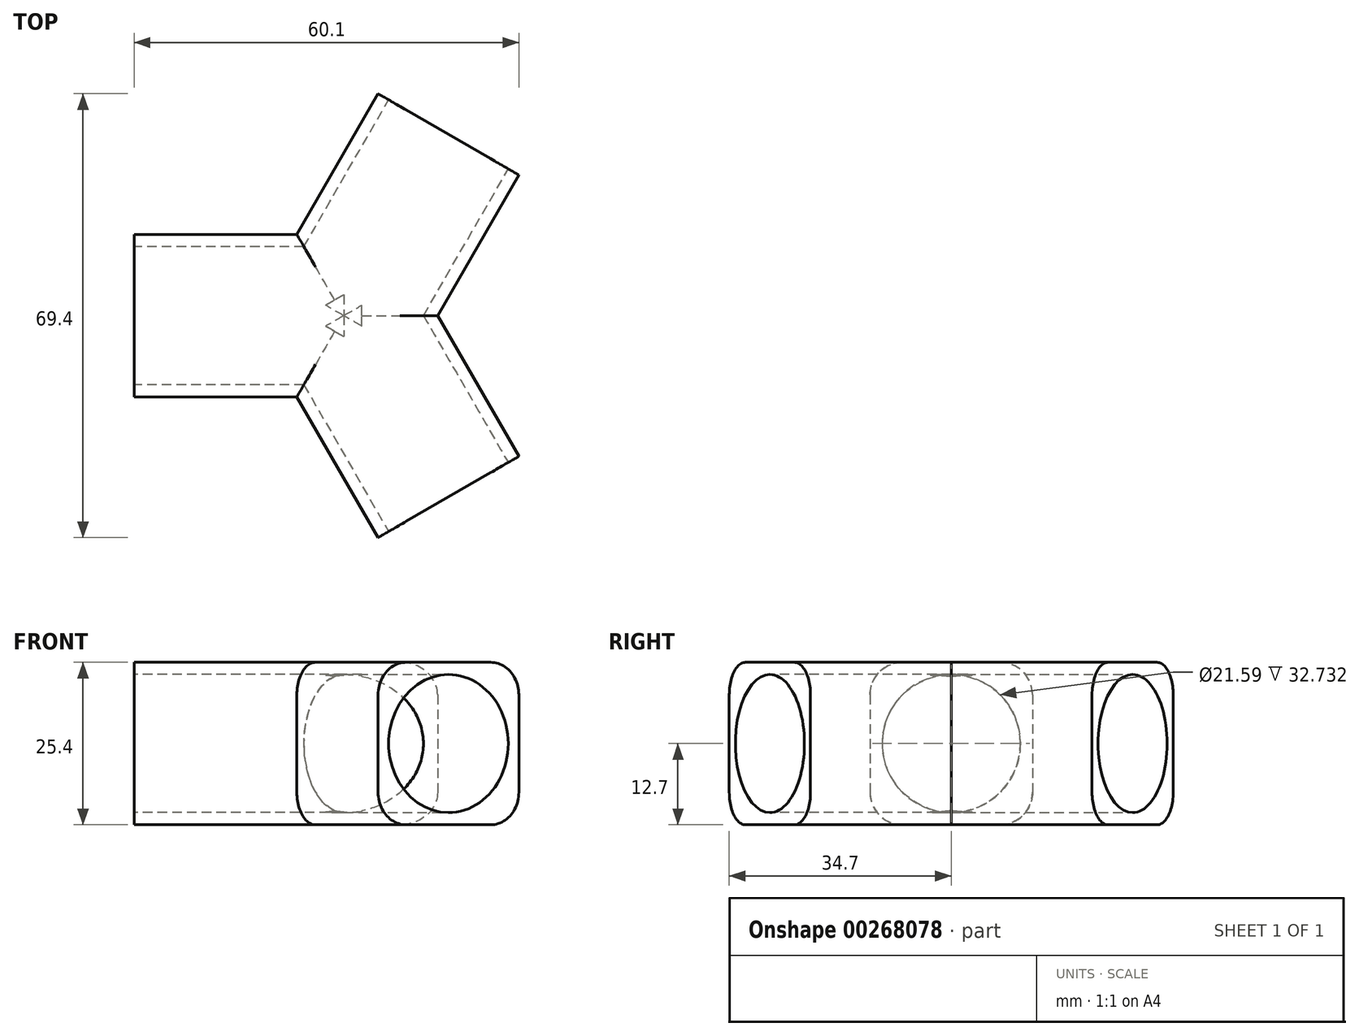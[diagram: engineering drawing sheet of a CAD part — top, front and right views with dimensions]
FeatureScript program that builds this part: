
annotation { "Feature Type Name" : "Feature", "Feature Type Description" : "" }
export const myFeature = defineFeature(function(context is Context, id is Id, definition is map)
    precondition{}
    {
        {
            var Q0;
            Q0=qCreatedBy(makeId("Top.planeOp"),FACE);
            var sketch = newSketch(context, id + "F0", { "sketchPlane" : qUnion([Q0])});
            skLineSegment(sketch, "E0.bottom", {"start": v(-5.96, 34.7) * mm, "end": v(16.04, 22) * mm});
            skLineSegment(sketch, "E0.top", {"start": v(-18.66, 12.7) * mm, "end": v(3.34, 0) * mm, "construction": true});
            skLineSegment(sketch, "E0.left", {"start": v(-5.96, 34.7) * mm, "end": v(-18.66, 12.7) * mm});
            skLineSegment(sketch, "E0.right", {"start": v(16.04, 22) * mm, "end": v(3.34, 0) * mm});
            skLineSegment(sketch, "E1.bottom", {"start": v(-44.06, 12.7) * mm, "end": v(-18.66, 12.7) * mm});
            skLineSegment(sketch, "E1.top", {"start": v(-44.06, -12.7) * mm, "end": v(-18.66, -12.7) * mm});
            skLineSegment(sketch, "E1.left", {"start": v(-44.06, 12.7) * mm, "end": v(-44.06, -12.7) * mm});
            skLineSegment(sketch, "E1.right", {"start": v(-18.66, 12.7) * mm, "end": v(-18.66, -12.7) * mm, "construction": true});
            skLineSegment(sketch, "E2.left", {"start": v(-18.66, -12.7) * mm, "end": v(3.34, 0) * mm, "construction": true});
            skLineSegment(sketch, "E3", {"start": v(-18.66, -12.7) * mm, "end": v(-5.96, -34.7) * mm});
            skLineSegment(sketch, "E4", {"start": v(-5.96, -34.7) * mm, "end": v(16.04, -22) * mm});
            skLineSegment(sketch, "E5", {"start": v(16.04, -22) * mm, "end": v(3.34, 0) * mm});
            skSolve(sketch);
        }
        {
            var Q0;
            Q0=makeQuery(id+"F0.imprint","IMPRINT",FACE,{"disambiguationData":[TD([[makeQuery(id+"F0.imprint","IMPRINT",EDGE,{"derivedFrom":sQuery(id+"F0.wireOp",EDGE,"E0.bottom")}),-1.0]])]});
            extrude(context, id + "F1", {"entities" : qUnion([Q0]), "depth" : 25.4 * mm});
        }
        {
            var Q0;
            Q0=makeQuery(id+"F1.opExtrude","SWEPT_FACE",FACE,{"disambiguationData":[OSD([sQuery(id+"F0.wireOp",EDGE,"E4")])]});
            var sketch = newSketch(context, id + "F2", { "sketchPlane" : qUnion([Q0])});
            skLineSegment(sketch, "E6", {"start": v(-9.8, 0) * mm, "end": v(-9.8, 25.4) * mm, "construction": true});
            skCircle(sketch, "E7", {"center": v(-9.8, 12.7) * mm, "radius": 10.8 * mm});
            skSolve(sketch);
        }
        {
            var Q0;
            Q0=makeQuery(id+"F1.opExtrude","SWEPT_FACE",FACE,{"disambiguationData":[OSD([sQuery(id+"F0.wireOp",EDGE,"E0.bottom")])]});
            var sketch = newSketch(context, id + "F3", { "sketchPlane" : qUnion([Q0])});
            skLineSegment(sketch, "E8", {"start": v(9.8, 0) * mm, "end": v(9.8, 25.4) * mm, "construction": true});
            skCircle(sketch, "E9", {"center": v(9.8, 12.7) * mm, "radius": 10.8 * mm});
            skSolve(sketch);
        }
        {
            var Q0;
            Q0=makeQuery(id+"F1.opExtrude","SWEPT_FACE",FACE,{"disambiguationData":[OSD([sQuery(id+"F0.wireOp",EDGE,"E1.left")])]});
            var sketch = newSketch(context, id + "F4", { "sketchPlane" : qUnion([Q0])});
            skLineSegment(sketch, "E10", {"start": v(0, 0) * mm, "end": v(0, 25.4) * mm, "construction": true});
            skCircle(sketch, "E11", {"center": v(0, 12.7) * mm, "radius": 10.8 * mm});
            skSolve(sketch);
        }
        {
            var Q0;
            Q0=makeQuery(id+"F4.imprint","IMPRINT",FACE,{"disambiguationData":[TD([[makeQuery(id+"F4.imprint","IMPRINT",EDGE,{"derivedFrom":sQuery(id+"F4.wireOp",EDGE,"E11")}),1.0]])]});
            extrude(context, id + "F5", {"entities" : qUnion([Q0]), "operationType" : NewBodyOperationType.REMOVE, "oppositeDirection" : true, "depth" : 35.56 * mm});
        }
        {
            var Q0;
            Q0=makeQuery(id+"F3.imprint","IMPRINT",FACE,{"disambiguationData":[TD([[makeQuery(id+"F3.imprint","IMPRINT",EDGE,{"derivedFrom":sQuery(id+"F3.wireOp",EDGE,"E9")}),1.0]])]});
            extrude(context, id + "F6", {"entities" : qUnion([Q0]), "operationType" : NewBodyOperationType.REMOVE, "oppositeDirection" : true, "depth" : 35.56 * mm});
        }
        {
            var Q0;
            Q0=makeQuery(id+"F2.imprint","IMPRINT",FACE,{"disambiguationData":[TD([[makeQuery(id+"F2.imprint","IMPRINT",EDGE,{"derivedFrom":sQuery(id+"F2.wireOp",EDGE,"E7")}),1.0]])]});
            extrude(context, id + "F7", {"entities" : qUnion([Q0]), "operationType" : NewBodyOperationType.REMOVE, "oppositeDirection" : true, "depth" : 35.56 * mm});
        }
        {
            var Q0;
            Q0=makeQuery(id+"F1.opExtrude","CAP_EDGE",EDGE,{"disambiguationData":[OSD([sQuery(id+"F0.wireOp",EDGE,"E1.top")])],"isStart":false});
            var Q1;
            Q1=makeQuery(id+"F1.opExtrude","CAP_EDGE",EDGE,{"disambiguationData":[OSD([sQuery(id+"F0.wireOp",EDGE,"E3")])],"isStart":false});
            var Q2;
            Q2=makeQuery(id+"F1.opExtrude","CAP_EDGE",EDGE,{"disambiguationData":[OSD([sQuery(id+"F0.wireOp",EDGE,"E1.bottom")])],"isStart":false});
            var Q3;
            Q3=makeQuery(id+"F1.opExtrude","CAP_EDGE",EDGE,{"disambiguationData":[OSD([sQuery(id+"F0.wireOp",EDGE,"E0.left")])],"isStart":false});
            var Q4;
            Q4=makeQuery(id+"F1.opExtrude","CAP_EDGE",EDGE,{"disambiguationData":[OSD([sQuery(id+"F0.wireOp",EDGE,"E0.right")])],"isStart":false});
            var Q5;
            Q5=makeQuery(id+"F1.opExtrude","CAP_EDGE",EDGE,{"disambiguationData":[OSD([sQuery(id+"F0.wireOp",EDGE,"E5")])],"isStart":false});
            var Q6;
            Q6=makeQuery(id+"F1.opExtrude","CAP_EDGE",EDGE,{"disambiguationData":[OSD([sQuery(id+"F0.wireOp",EDGE,"E1.top")])],"isStart":true});
            var Q7;
            Q7=makeQuery(id+"F1.opExtrude","CAP_EDGE",EDGE,{"disambiguationData":[OSD([sQuery(id+"F0.wireOp",EDGE,"E3")])],"isStart":true});
            var Q8;
            Q8=makeQuery(id+"F1.opExtrude","CAP_EDGE",EDGE,{"disambiguationData":[OSD([sQuery(id+"F0.wireOp",EDGE,"E5")])],"isStart":true});
            var Q9;
            Q9=makeQuery(id+"F1.opExtrude","CAP_EDGE",EDGE,{"disambiguationData":[OSD([sQuery(id+"F0.wireOp",EDGE,"E0.right")])],"isStart":true});
            var Q10;
            Q10=makeQuery(id+"F1.opExtrude","CAP_EDGE",EDGE,{"disambiguationData":[OSD([sQuery(id+"F0.wireOp",EDGE,"E1.bottom")])],"isStart":true});
            var Q11;
            Q11=makeQuery(id+"F1.opExtrude","CAP_EDGE",EDGE,{"disambiguationData":[OSD([sQuery(id+"F0.wireOp",EDGE,"E0.left")])],"isStart":true});
            fillet(context, id + "F8", {"entities" : qUnion([Q0, Q1, Q2, Q3, Q4, Q5, Q6, Q7, Q8, Q9, Q10, Q11]), "radius" : 5.08 * mm, "tangentPropagation" : true, "allowEdgeOverflow" : false});
        }
    });
